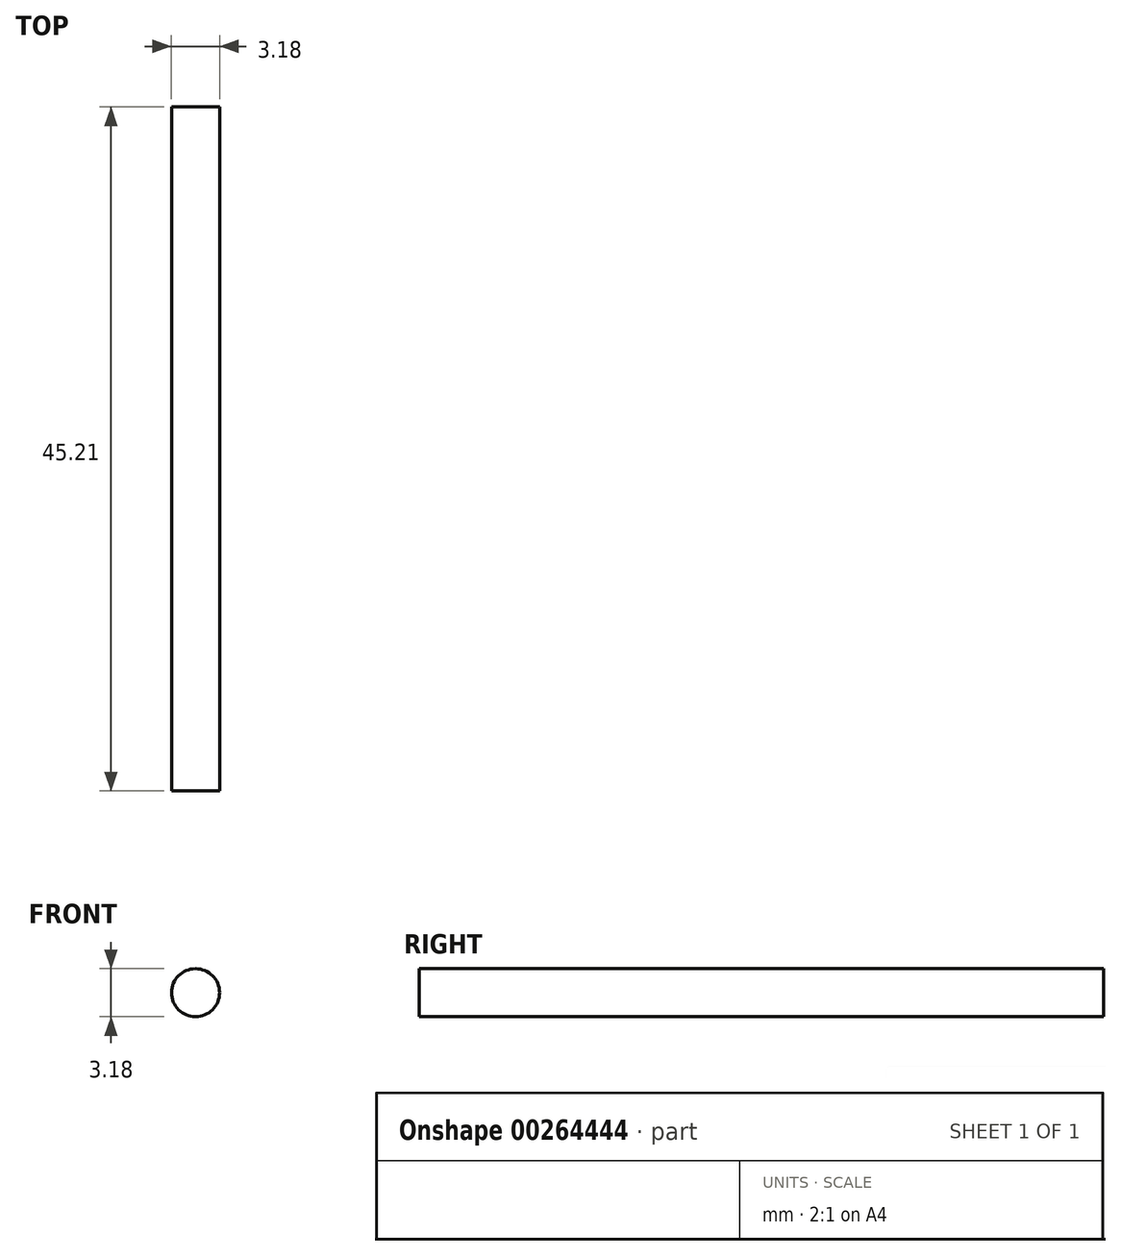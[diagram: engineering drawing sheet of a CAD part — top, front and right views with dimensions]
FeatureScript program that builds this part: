
annotation { "Feature Type Name" : "Feature", "Feature Type Description" : "" }
export const myFeature = defineFeature(function(context is Context, id is Id, definition is map)
    precondition{}
    {
        {
            var Q0;
            Q0=qCreatedBy(makeId("Front.planeOp"),FACE);
            var sketch = newSketch(context, id + "F0", { "sketchPlane" : qUnion([Q0])});
            skCircle(sketch, "E0", {"center": v(0, 0) * mm, "radius": 1.59 * mm});
            skSolve(sketch);
        }
        {
            var Q0;
            Q0=qSketchRegion(id+"F0",true);
            extrude(context, id + "F1", {"entities" : qUnion([Q0]), "depth" : 45.2 * mm});
        }
    });
